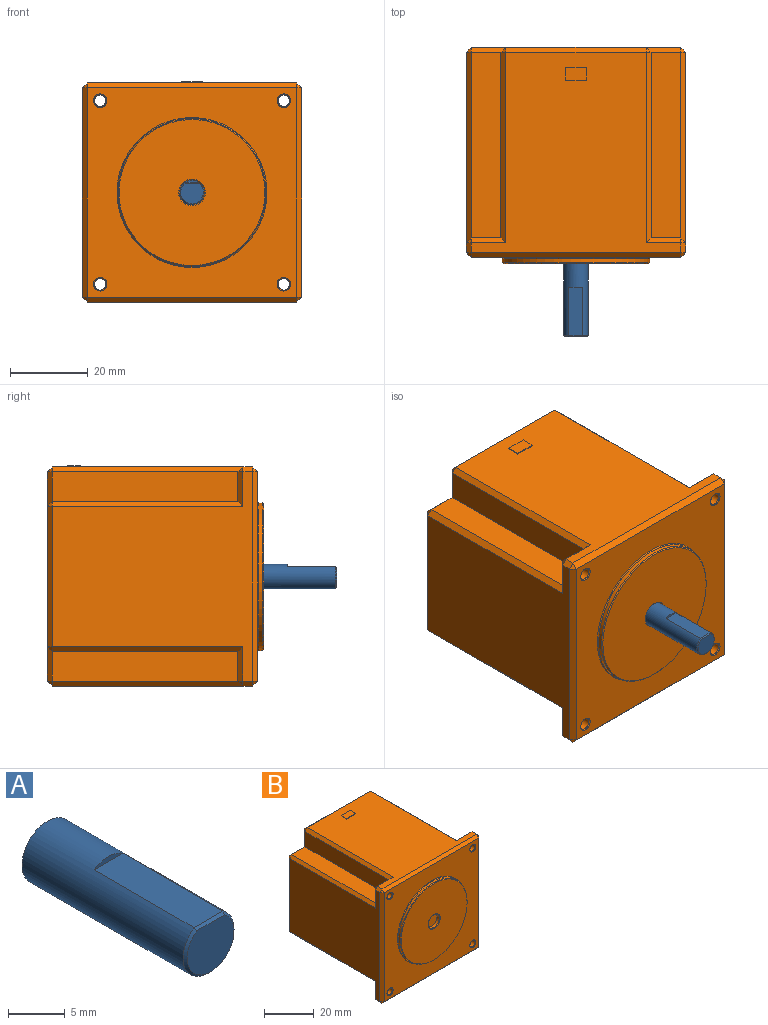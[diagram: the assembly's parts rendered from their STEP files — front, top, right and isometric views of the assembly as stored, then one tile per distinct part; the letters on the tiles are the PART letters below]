
ASSEMBLY  parts=2 mates=1
PART A: 7 faces, bbox 6.4x20.3x6.4 mm
  f0: cylinder r=3.17mm len=20.07mm, axis (0,1,0), area 352.7mm2, adj f2,f3,f4,f5
  f1: plane 5.84x5.28mm, normal (0,-1,0), area 25.5mm2, adj f5,f6
  f2: plane 6.35x6.35mm, normal (0,1,0), area 31.7mm2, adj f0
  f3: plane 12.45x3.6mm, normal (0,0,1), area 44.8mm2, adj f0,f4,f6
  f4: plane 3.6x0.56mm, normal (0,-1,0), area 1.4mm2, adj f0,f3
  f5: cone r=2.92mm half-angle=45deg, axis (0,1,0), area 5.5mm2, adj f0,f1,f6
  f6: plane 3.6x0.26mm, normal (0,-0.71,0.71), area 1.3mm2, adj f1,f3,f5
PART B: 94 faces, bbox 56.4x55.6x56.6 mm
  f0: plane 53.85x51.56mm, normal (0,0,1), area 1887.9mm2, adj f27,f28,f31,f36,f41,f42,f43,f44
  f1: plane 53.85x51.56mm, normal (0,0,-1), area 1904.9mm2, adj f48,f49,f59,f60,f64,f69,f72,f73
  f2: plane 53.85x51.56mm, normal (1,0,0), area 1904.9mm2, adj f41,f50,f56,f60,f61,f66,f70,f71
  f3: plane 53.85x51.56mm, normal (-1,0,0), area 1904.9mm2, adj f27,f29,f34,f35,f45,f46,f47,f48
  f4: plane 53.85x53.85mm, normal (0,1,0), area 2583.5mm2, adj f32,f33,f44,f45,f57,f58,f62,f63
  f5: cylinder r=1.49mm len=4.57mm, axis (0,-1,0), area 42.7mm2, adj f82,f88
  f6: cylinder r=1.49mm len=4.57mm, axis (0,-1,0), area 42.7mm2, adj f83,f86
  f7: cylinder r=1.49mm len=4.57mm, axis (0,-1,0), area 42.7mm2, adj f84,f85
  f8: cylinder r=1.49mm len=4.57mm, axis (0,-1,0), area 42.7mm2, adj f81,f87
  f9: plane 53.85x53.85mm, normal (0,-1,0), area 1690.9mm2, adj f35,f36,f49,f50,f80,f81,f82,f83
  f10: cylinder r=3.17mm len=6.35mm, axis (0,1,0), area 25.3mm2, adj f13,f78
  f11: cylinder r=19.05mm len=38.1mm, axis (0,1,0), area 121.6mm2, adj f79,f80
  f12: plane 37.59x37.59mm, normal (0,-1,0), area 1073mm2, adj f78,f79
  f13: plane 6.35x6.35mm, normal (0,-1,0), area 31.7mm2, adj f10
  f14: plane 7.62x7.62mm, normal (0,1,0), area 48.6mm2, adj f15,f16,f47,f59,f87
  f15: plane 47.75x7.62mm, normal (-1,0,0), area 363.9mm2, adj f14,f16,f63,f64
  f16: plane 47.75x7.62mm, normal (0,0,-1), area 363.9mm2, adj f14,f15,f46,f58
  f17: plane 7.62x7.62mm, normal (0,1,0), area 48.6mm2, adj f18,f19,f66,f69,f85
  f18: plane 47.75x7.62mm, normal (1,0,0), area 363.9mm2, adj f17,f19,f73,f77
  f19: plane 47.75x7.62mm, normal (0,0,-1), area 363.9mm2, adj f17,f18,f70,f76
  f20: plane 7.62x7.62mm, normal (0,1,0), area 48.6mm2, adj f21,f22,f42,f56,f86
  f21: plane 47.75x7.62mm, normal (1,0,0), area 363.9mm2, adj f20,f22,f43,f57
  f22: plane 47.75x7.62mm, normal (0,0,1), area 363.9mm2, adj f20,f21,f61,f62
  f23: plane 7.62x7.62mm, normal (0,1,0), area 48.6mm2, adj f24,f25,f28,f29,f88
  f24: plane 47.75x7.62mm, normal (-1,0,0), area 363.9mm2, adj f23,f25,f31,f32
  f25: plane 47.75x7.62mm, normal (0,0,1), area 363.9mm2, adj f23,f24,f33,f34
  f26: plane 1.27x1.27mm, normal (-0.58,0.58,0.58), area 1.4mm2, adj f27,f28,f29
  f27: plane 2.54x1.27mm, normal (-0.71,0,0.71), area 4.6mm2, adj f0,f3,f26,f30
  f28: plane 8.89x1.27mm, normal (0,0.71,0.71), area 14.8mm2, adj f0,f23,f26,f31
  f29: plane 8.89x1.27mm, normal (-0.71,0.71,0), area 14.8mm2, adj f3,f23,f26,f34
  f30: plane 1.27x1.27mm, normal (-0.58,-0.58,0.58), area 1.4mm2, adj f27,f35,f36
  f31: plane 49.02x1.27mm, normal (-0.71,0,0.71), area 86.9mm2, adj f0,f24,f28,f37
  f32: plane 8.89x1.27mm, normal (-0.71,0.71,0), area 14.8mm2, adj f4,f24,f33,f37
  f33: plane 8.89x1.27mm, normal (0,0.71,0.71), area 14.8mm2, adj f4,f25,f32,f38
  f34: plane 49.02x1.27mm, normal (-0.71,0,0.71), area 86.9mm2, adj f3,f25,f29,f38
  f35: plane 53.85x1.27mm, normal (-0.71,-0.71,0), area 96.7mm2, adj f3,f9,f30,f39
  f36: plane 53.85x1.27mm, normal (0,-0.71,0.71), area 96.7mm2, adj f0,f9,f30,f40
  f37: plane 1.27x1.27mm, normal (-0.58,0.58,0.58), area 1.4mm2, adj f31,f32,f44
  f38: plane 1.27x1.27mm, normal (-0.58,0.58,0.58), area 1.4mm2, adj f33,f34,f45
  f39: plane 1.27x1.27mm, normal (-0.58,-0.58,-0.58), area 1.4mm2, adj f35,f48,f49
  f40: plane 1.27x1.27mm, normal (0.58,-0.58,0.58), area 1.4mm2, adj f36,f41,f50
  f41: plane 2.54x1.27mm, normal (0.71,0,0.71), area 4.6mm2, adj f0,f2,f40,f51
  f42: plane 8.89x1.27mm, normal (0,0.71,0.71), area 14.8mm2, adj f0,f20,f43,f51
  f43: plane 49.02x1.27mm, normal (0.71,0,0.71), area 86.9mm2, adj f0,f21,f42,f52
  f44: plane 36.07x1.27mm, normal (0,0.71,0.71), area 64.8mm2, adj f0,f4,f37,f52
  f45: plane 36.07x1.27mm, normal (-0.71,0.71,0), area 64.8mm2, adj f3,f4,f38,f53
  f46: plane 49.02x1.27mm, normal (-0.71,0,-0.71), area 86.9mm2, adj f3,f16,f47,f53
  f47: plane 8.89x1.27mm, normal (-0.71,0.71,0), area 14.8mm2, adj f3,f14,f46,f54
  f48: plane 2.54x1.27mm, normal (-0.71,0,-0.71), area 4.6mm2, adj f1,f3,f39,f54
  f49: plane 53.85x1.27mm, normal (0,-0.71,-0.71), area 96.7mm2, adj f1,f9,f39,f55
  f50: plane 53.85x1.27mm, normal (0.71,-0.71,0), area 96.7mm2, adj f2,f9,f40,f55
  f51: plane 1.27x1.27mm, normal (0.58,0.58,0.58), area 1.4mm2, adj f41,f42,f56
  f52: plane 1.27x1.27mm, normal (0.58,0.58,0.58), area 1.4mm2, adj f43,f44,f57
  f53: plane 1.27x1.27mm, normal (-0.58,0.58,-0.58), area 1.4mm2, adj f45,f46,f58
  f54: plane 1.27x1.27mm, normal (-0.58,0.58,-0.58), area 1.4mm2, adj f47,f48,f59
  f55: plane 1.27x1.27mm, normal (0.58,-0.58,-0.58), area 1.4mm2, adj f49,f50,f60
  f56: plane 8.89x1.27mm, normal (0.71,0.71,0), area 14.8mm2, adj f2,f20,f51,f61
  f57: plane 8.89x1.27mm, normal (0.71,0.71,0), area 14.8mm2, adj f4,f21,f52,f62
  f58: plane 8.89x1.27mm, normal (0,0.71,-0.71), area 14.8mm2, adj f4,f16,f53,f63
  f59: plane 8.89x1.27mm, normal (0,0.71,-0.71), area 14.8mm2, adj f1,f14,f54,f64
  f60: plane 2.54x1.27mm, normal (0.71,0,-0.71), area 4.6mm2, adj f1,f2,f55,f65
  f61: plane 49.02x1.27mm, normal (0.71,0,0.71), area 86.9mm2, adj f2,f22,f56,f67
  f62: plane 8.89x1.27mm, normal (0,0.71,0.71), area 14.8mm2, adj f4,f22,f57,f67
  f63: plane 8.89x1.27mm, normal (-0.71,0.71,0), area 14.8mm2, adj f4,f15,f58,f68
  f64: plane 49.02x1.27mm, normal (-0.71,0,-0.71), area 86.9mm2, adj f1,f15,f59,f68
  f65: plane 1.27x1.27mm, normal (0.58,0.58,-0.58), area 1.4mm2, adj f60,f66,f69
  f66: plane 8.89x1.27mm, normal (0.71,0.71,0), area 14.8mm2, adj f2,f17,f65,f70
  f67: plane 1.27x1.27mm, normal (0.58,0.58,0.58), area 1.4mm2, adj f61,f62,f71
  f68: plane 1.27x1.27mm, normal (-0.58,0.58,-0.58), area 1.4mm2, adj f63,f64,f72
  f69: plane 8.89x1.27mm, normal (0,0.71,-0.71), area 14.8mm2, adj f1,f17,f65,f73
  f70: plane 49.02x1.27mm, normal (0.71,0,-0.71), area 86.9mm2, adj f2,f19,f66,f74
  f71: plane 36.07x1.27mm, normal (0.71,0.71,0), area 64.8mm2, adj f2,f4,f67,f74
  f72: plane 36.07x1.27mm, normal (0,0.71,-0.71), area 64.8mm2, adj f1,f4,f68,f75
  f73: plane 49.02x1.27mm, normal (0.71,0,-0.71), area 86.9mm2, adj f1,f18,f69,f75
  f74: plane 1.27x1.27mm, normal (0.58,0.58,-0.58), area 1.4mm2, adj f70,f71,f76
  f75: plane 1.27x1.27mm, normal (0.58,0.58,-0.58), area 1.4mm2, adj f72,f73,f77
  f76: plane 8.89x1.27mm, normal (0,0.71,-0.71), area 14.8mm2, adj f4,f19,f74,f77
  f77: plane 8.89x1.27mm, normal (0.71,0.71,0), area 14.8mm2, adj f4,f18,f75,f76
  f78: cone r=3.17mm half-angle=45deg, axis (0,-1,0), area 7.5mm2, adj f10,f12
  f79: cone r=18.8mm half-angle=45deg, axis (0,1,0), area 42.7mm2, adj f11,f12
  f80: cone r=19.05mm half-angle=45deg, axis (0,1,0), area 43.3mm2, adj f9,f11
  f81: cone r=1.49mm half-angle=45deg, axis (0,-1,0), area 3.6mm2, adj f8,f9
  f82: cone r=1.49mm half-angle=45deg, axis (0,-1,0), area 3.6mm2, adj f5,f9
  f83: cone r=1.49mm half-angle=45deg, axis (0,-1,0), area 3.6mm2, adj f6,f9
  f84: cone r=1.49mm half-angle=45deg, axis (0,-1,0), area 3.6mm2, adj f7,f9
  f85: cone r=1.74mm half-angle=45deg, axis (0,1,0), area 3.6mm2, adj f7,f17
  f86: cone r=1.74mm half-angle=45deg, axis (0,1,0), area 3.6mm2, adj f6,f20
  f87: cone r=1.74mm half-angle=45deg, axis (0,1,0), area 3.6mm2, adj f8,f14
  f88: cone r=1.74mm half-angle=45deg, axis (0,1,0), area 3.6mm2, adj f5,f23
  f89: plane 5.22x0.25mm, normal (0,-1,0), area 1.3mm2, adj f0,f90,f92,f93
  f90: plane 3.27x0.25mm, normal (1,0,0), area 0.8mm2, adj f0,f89,f91,f93
  f91: plane 5.22x0.25mm, normal (0,1,0), area 1.3mm2, adj f0,f90,f92,f93
  f92: plane 3.27x0.25mm, normal (-1,0,0), area 0.8mm2, adj f0,f89,f91,f93
  f93: plane 5.22x3.27mm, normal (0,0,1), area 17mm2, adj f89,f90,f91,f92
PLACE A rot(axis=(0,-1,0),1.9deg) t=(0,0,0)mm
PLACE B at identity
MATE cylindrical A.f0 <-> B.f10  axis (0,-1,0) through (0,0,0)mm
